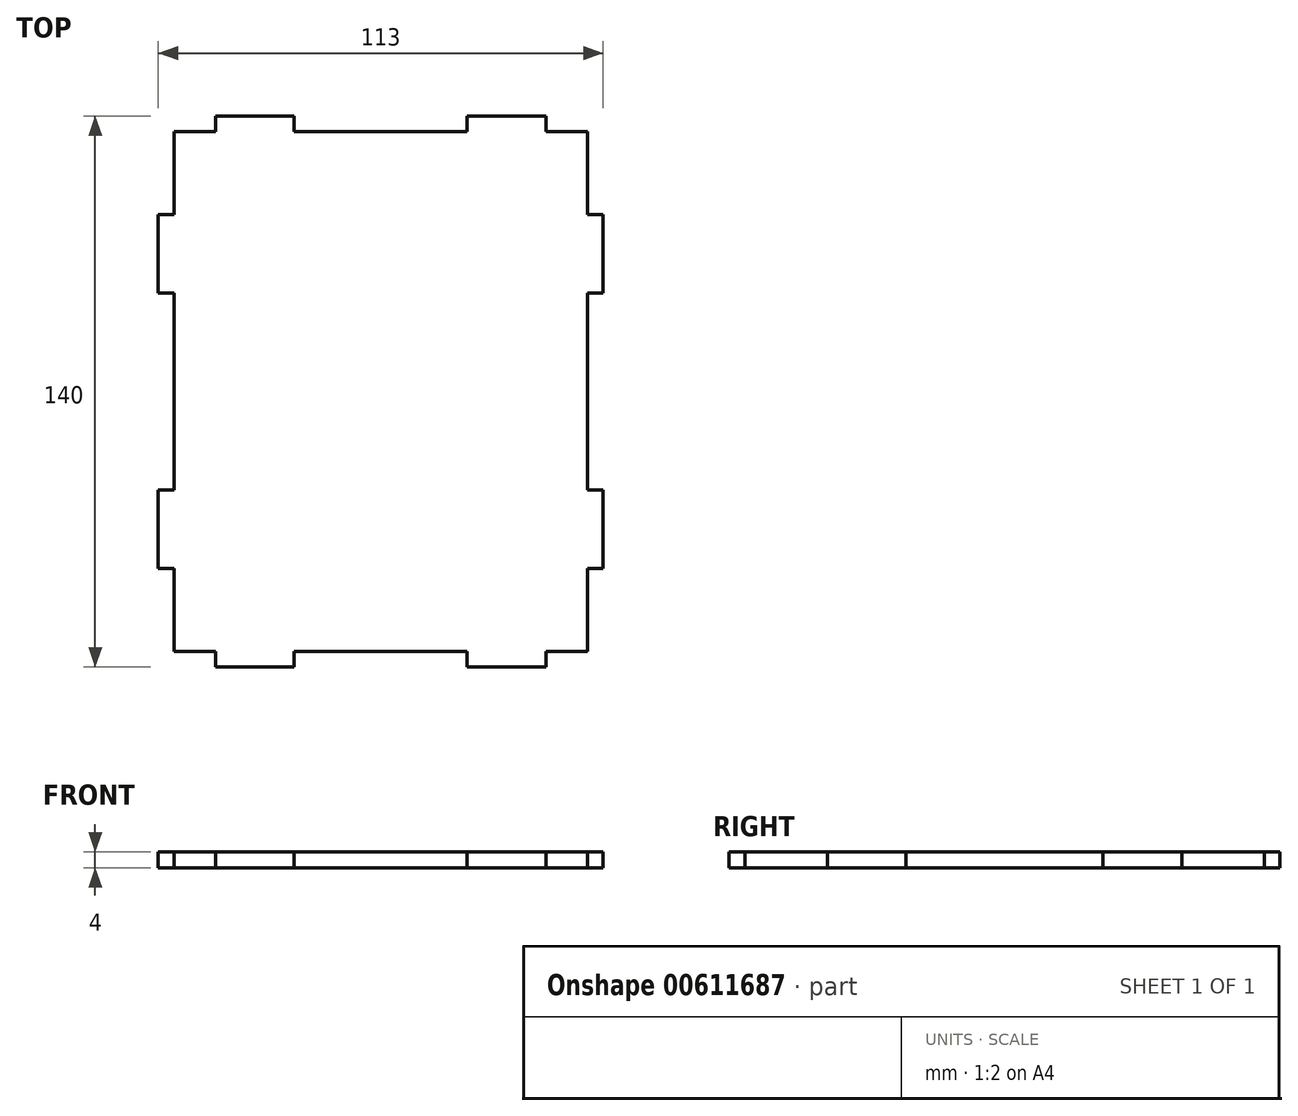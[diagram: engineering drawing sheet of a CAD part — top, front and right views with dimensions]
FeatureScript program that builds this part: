
annotation { "Feature Type Name" : "Feature", "Feature Type Description" : "" }
export const myFeature = defineFeature(function(context is Context, id is Id, definition is map)
    precondition{}
    {
        {
            var Q0;
            Q0=qCreatedBy(makeId("Top.planeOp"),FACE);
            var sketch = newSketch(context, id + "F0", { "sketchPlane" : qUnion([Q0])});
            skLineSegment(sketch, "E0.bottom", {"start": v(52.5, 66) * mm, "end": v(42, 66) * mm});
            skLineSegment(sketch, "E0.top", {"start": v(52.5, -66) * mm, "end": v(42, -66) * mm});
            skLineSegment(sketch, "E0.left", {"start": v(52.5, 66) * mm, "end": v(52.5, 45) * mm});
            skLineSegment(sketch, "E0.right", {"start": v(-52.5, 66) * mm, "end": v(-52.5, 45) * mm});
            skPoint(sketch, "E0.middle", {"position": v(0, 0) * mm});
            skLineSegment(sketch, "E1.bottom", {"start": v(-52.5, 45) * mm, "end": v(-56.5, 45) * mm});
            skLineSegment(sketch, "E1.top", {"start": v(-52.5, 25) * mm, "end": v(-56.5, 25) * mm});
            skLineSegment(sketch, "E1.right", {"start": v(-56.5, 45) * mm, "end": v(-56.5, 25) * mm});
            skLineSegment(sketch, "E2.MirrorCS", {"start": v(52.5, 45) * mm, "end": v(56.5, 45) * mm});
            skLineSegment(sketch, "E3.MirrorCS", {"start": v(52.5, 25) * mm, "end": v(56.5, 25) * mm});
            skLineSegment(sketch, "E4.MirrorCS", {"start": v(56.5, 45) * mm, "end": v(56.5, 25) * mm});
            skLineSegment(sketch, "E5.MirrorCS", {"start": v(52.5, -45) * mm, "end": v(56.5, -45) * mm});
            skLineSegment(sketch, "E6.MirrorCS", {"start": v(52.5, -25) * mm, "end": v(56.5, -25) * mm});
            skLineSegment(sketch, "E7.MirrorCS", {"start": v(-52.5, -25) * mm, "end": v(-56.5, -25) * mm});
            skLineSegment(sketch, "E8.MirrorCS", {"start": v(-52.5, -45) * mm, "end": v(-56.5, -45) * mm});
            skLineSegment(sketch, "E9.MirrorCS", {"start": v(56.5, -45) * mm, "end": v(56.5, -25) * mm});
            skLineSegment(sketch, "E10.MirrorCS", {"start": v(-56.5, -45) * mm, "end": v(-56.5, -25) * mm});
            skLineSegment(sketch, "E11.trimOffspring", {"start": v(-52.5, 25) * mm, "end": v(-52.5, -25) * mm});
            skLineSegment(sketch, "E12.trimOffspring", {"start": v(52.5, 25) * mm, "end": v(52.5, -25) * mm});
            skLineSegment(sketch, "E13.trimOffspring", {"start": v(52.5, -45) * mm, "end": v(52.5, -66) * mm});
            skLineSegment(sketch, "E14.trimOffspring", {"start": v(-52.5, -45) * mm, "end": v(-52.5, -66) * mm});
            skLineSegment(sketch, "E15.top", {"start": v(-42, 70) * mm, "end": v(-22, 70) * mm});
            skLineSegment(sketch, "E15.left", {"start": v(-42, 66) * mm, "end": v(-42, 70) * mm});
            skLineSegment(sketch, "E15.right", {"start": v(-22, 66) * mm, "end": v(-22, 70) * mm});
            skLineSegment(sketch, "E16.trimOffspring", {"start": v(-42, 66) * mm, "end": v(-52.5, 66) * mm});
            skLineSegment(sketch, "E17.MirrorCS", {"start": v(42, 70) * mm, "end": v(22, 70) * mm});
            skLineSegment(sketch, "E18.MirrorCS", {"start": v(42, 66) * mm, "end": v(42, 70) * mm});
            skLineSegment(sketch, "E19.MirrorCS", {"start": v(22, 66) * mm, "end": v(22, 70) * mm});
            skLineSegment(sketch, "E20.trimOffspring", {"start": v(22, 66) * mm, "end": v(-22, 66) * mm});
            skLineSegment(sketch, "E21.MirrorCS", {"start": v(42, -70) * mm, "end": v(22, -70) * mm});
            skLineSegment(sketch, "E22.MirrorCS", {"start": v(42, -66) * mm, "end": v(42, -70) * mm});
            skLineSegment(sketch, "E23.MirrorCS", {"start": v(22, -66) * mm, "end": v(22, -70) * mm});
            skLineSegment(sketch, "E24.MirrorCS", {"start": v(-22, -66) * mm, "end": v(-22, -70) * mm});
            skLineSegment(sketch, "E25.MirrorCS", {"start": v(-42, -70) * mm, "end": v(-22, -70) * mm});
            skLineSegment(sketch, "E26.MirrorCS", {"start": v(-42, -66) * mm, "end": v(-42, -70) * mm});
            skLineSegment(sketch, "E27.trimOffspring", {"start": v(-42, -66) * mm, "end": v(-52.5, -66) * mm});
            skLineSegment(sketch, "E28.trimOffspring", {"start": v(22, -66) * mm, "end": v(-22, -66) * mm});
            skSolve(sketch);
        }
        {
            var Q0;
            Q0=makeQuery(id+"F0.imprint","IMPRINT",FACE,{"disambiguationData":[TD([[makeQuery(id+"F0.imprint","IMPRINT",EDGE,{"derivedFrom":sQuery(id+"F0.wireOp",EDGE,"tXzo0Muj-3qYD-Yrpu-env9-NPLb1Lz4Y9nM.bottom")}),1.0]])]});
            var Q1;
            Q1=makeQuery(id+"F0.imprint","IMPRINT",FACE,{"disambiguationData":[TD([[makeQuery(id+"F0.imprint","IMPRINT",EDGE,{"derivedFrom":sQuery(id+"F0.wireOp",EDGE,"E0.bottom")}),1.0]])]});
            extrude(context, id + "F1", {"entities" : qUnion([Q0, Q1]), "depth" : 4 * mm, "offsetDistance" : 25 * mm});
        }
    });
